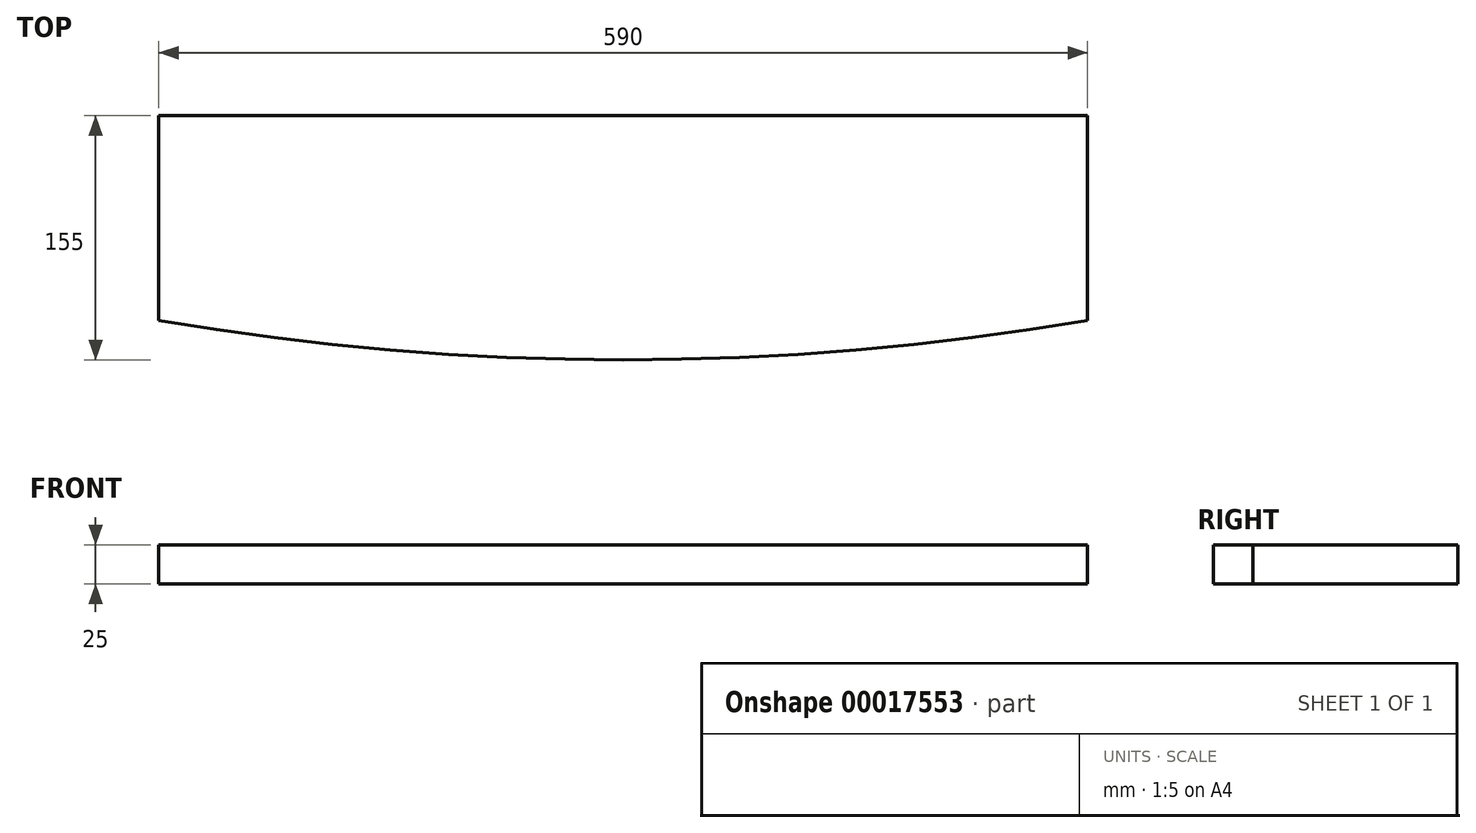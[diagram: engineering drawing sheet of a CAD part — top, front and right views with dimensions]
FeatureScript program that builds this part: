
annotation { "Feature Type Name" : "Feature", "Feature Type Description" : "" }
export const myFeature = defineFeature(function(context is Context, id is Id, definition is map)
    precondition{}
    {
        {
            var Q0;
            Q0=qCreatedBy(makeId("Top.planeOp"),FACE);
            var sketch = newSketch(context, id + "F0", { "sketchPlane" : qUnion([Q0])});
            skLineSegment(sketch, "E0.rect.bottom", {"start": v(-295, 12.5) * mm, "end": v(295, 12.5) * mm, "construction": true});
            skLineSegment(sketch, "E0.rect.top", {"start": v(-295, -12.5) * mm, "end": v(295, -12.5) * mm, "construction": true});
            skLineSegment(sketch, "E0.rect.left", {"start": v(-295, 12.5) * mm, "end": v(-295, -12.5) * mm, "construction": true});
            skLineSegment(sketch, "E0.rect.right", {"start": v(295, 12.5) * mm, "end": v(295, -12.5) * mm, "construction": true});
            skPoint(sketch, "E0.rect.middle", {"position": v(0, 0) * mm});
            skArc(sketch, "E1", {"start": v(-295, 12.5) * mm, "mid": v(0, -12.5) * mm, "end": v(295, 12.5) * mm});
            skLineSegment(sketch, "E2.top", {"start": v(-295, 142.5) * mm, "end": v(295, 142.5) * mm});
            skLineSegment(sketch, "E2.left", {"start": v(-295, 12.5) * mm, "end": v(-295, 142.5) * mm});
            skLineSegment(sketch, "E2.right", {"start": v(295, 12.5) * mm, "end": v(295, 142.5) * mm});
            skSolve(sketch);
        }
        {
            var Q0;
            Q0 = qSketchRegion(id + "F0", true);
            extrude(context, id + "F1", {"entities" : qUnion([Q0]), "depth" : 25 * mm});
        }
    });
